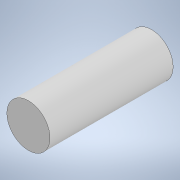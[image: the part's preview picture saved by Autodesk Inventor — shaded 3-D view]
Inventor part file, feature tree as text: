
AUTODESK INVENTOR PART (.ipt)
format: ipt  version: 2021 (Build 250183000, 183)  size: 90,112 bytes
history: native  units: mm
features: extrude x1, sketch x1
ambient origin geometry x8: Origin, YZ Plane, XZ Plane, XY Plane, X Axis, Y Axis, Z Axis, Center Point
bodies: Solid1 (feature_tree)
feature tree (2):
  extrude  "Extrusion1"  Depth=20.0mm TaperAngle=0.0deg
  sketch  "Sketch1"  dims[d0=7.0mm d1=20.0mm d2=0.0mm]
